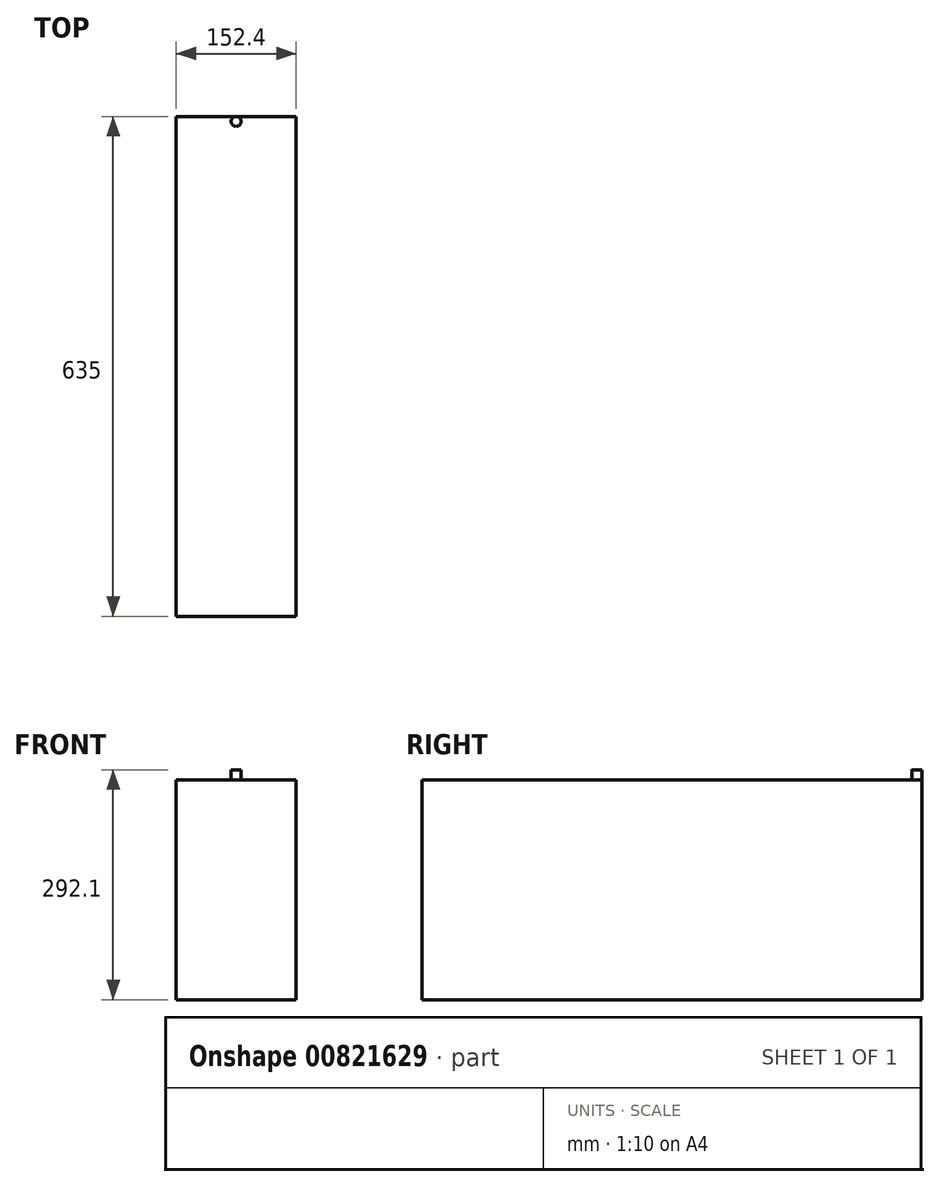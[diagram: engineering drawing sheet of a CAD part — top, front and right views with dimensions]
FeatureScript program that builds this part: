
annotation { "Feature Type Name" : "Feature", "Feature Type Description" : "" }
export const myFeature = defineFeature(function(context is Context, id is Id, definition is map)
    precondition{}
    {
        {
            var Q0;
            Q0=qCreatedBy(makeId("Top.planeOp"),FACE);
            var sketch = newSketch(context, id + "F0", { "sketchPlane" : qUnion([Q0])});
            skLineSegment(sketch, "E0", {"start": v(0, 2.13) * mm, "end": v(0, 637.13) * mm});
            skLineSegment(sketch, "E1", {"start": v(0, 2.13) * mm, "end": v(-152.4, 2.13) * mm});
            skLineSegment(sketch, "E2", {"start": v(0, 637.13) * mm, "end": v(-152.4, 637.13) * mm});
            skLineSegment(sketch, "E3", {"start": v(-152.4, 637.13) * mm, "end": v(-152.4, 2.13) * mm});
            skSolve(sketch);
        }
        {
            var Q0;
            Q0 = qSketchRegion(id + "F0", true);
            extrude(context, id + "F1", {"entities" : qUnion([Q0]), "depth" : 279.4 * mm, "offsetDistance" : 25.4 * mm});
        }
        {
            var Q0;
            Q0=makeQuery(id+"F1.opExtrude","CAP_FACE",FACE,{"disambiguationData":[OSD([sQuery(id+"F0.wireOp",EDGE,"E0"),sQuery(id+"F0.wireOp",EDGE,"E1"),sQuery(id+"F0.wireOp",EDGE,"E2"),sQuery(id+"F0.wireOp",EDGE,"E3")])],"isStart":false});
            var sketch = newSketch(context, id + "F2", { "sketchPlane" : qUnion([Q0])});
            skCircle(sketch, "E4", {"center": v(-76.2, 630.78) * mm, "radius": 6.35 * mm});
            skPoint(sketch, "E4.centerSnap0", {"position": v(-76.2, 637.13) * mm});
            skSolve(sketch);
        }
        {
            var Q0;
            Q0 = qSketchRegion(id + "F2", true);
            extrude(context, id + "F3", {"entities" : qUnion([Q0]), "operationType" : NewBodyOperationType.ADD, "depth" : 12.7 * mm, "offsetDistance" : 25.4 * mm});
        }
    });
